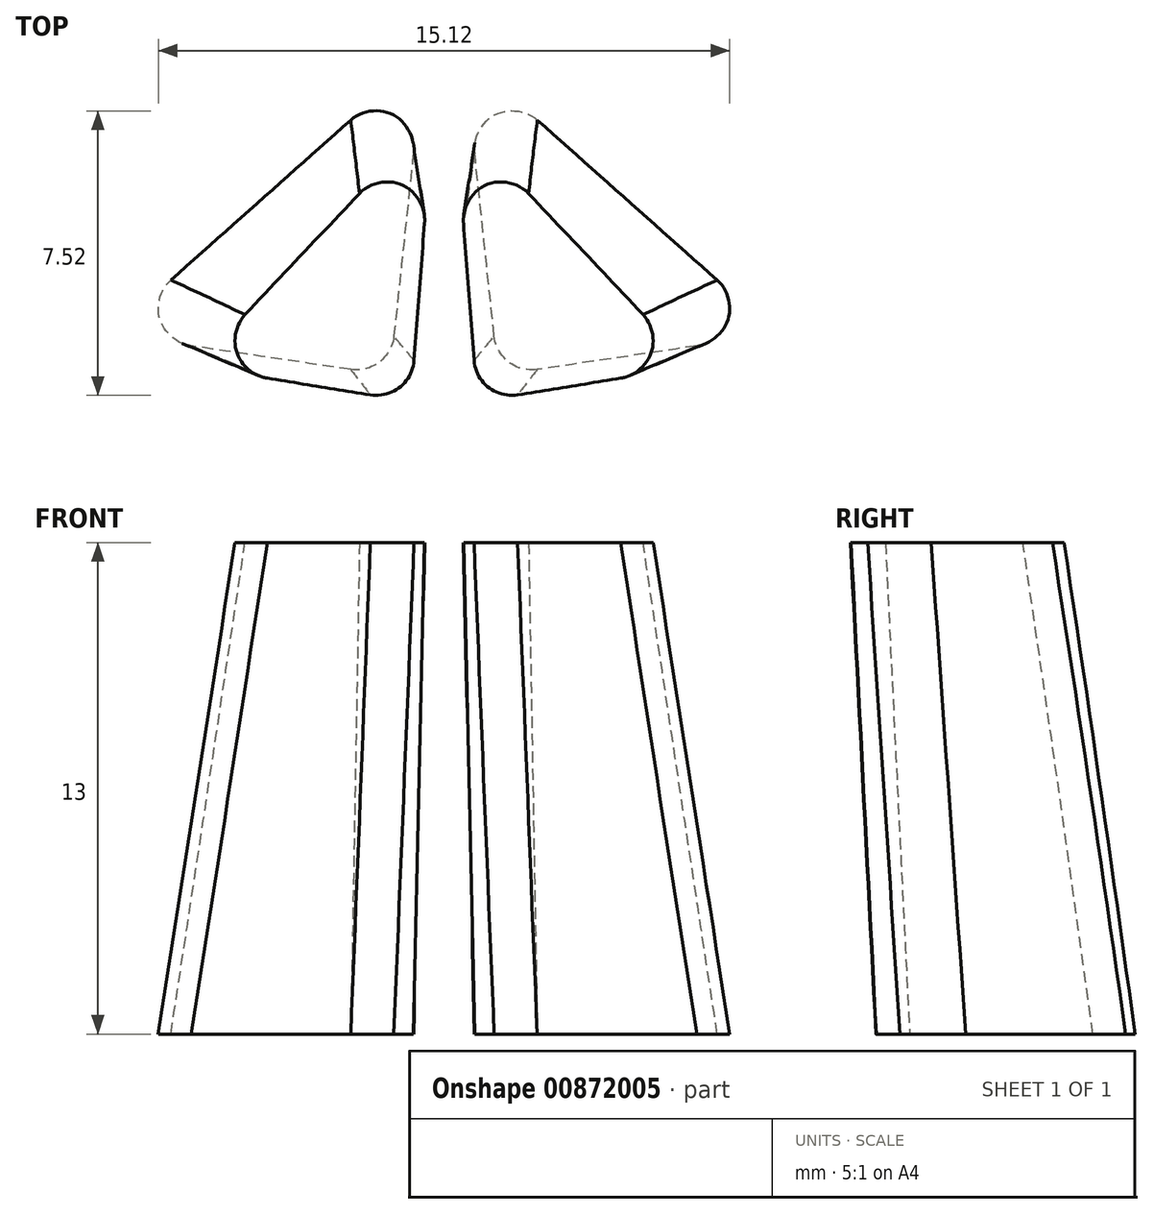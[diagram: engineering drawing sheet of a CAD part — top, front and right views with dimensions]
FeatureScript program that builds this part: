
annotation { "Feature Type Name" : "Feature", "Feature Type Description" : "" }
export const myFeature = defineFeature(function(context is Context, id is Id, definition is map)
    precondition{}
    {
        {
            var Q0;
            Q0=qCreatedBy(makeId("Top.planeOp"),FACE);
            var sketch = newSketch(context, id + "F0", { "sketchPlane" : qUnion([Q0])});
            skLineSegment(sketch, "E0", {"start": v(-1.48, -1.1) * mm, "end": v(-9, 0) * mm});
            skLineSegment(sketch, "E1", {"start": v(-9, 0) * mm, "end": v(-0.55, 7.43) * mm});
            skLineSegment(sketch, "E2", {"start": v(-0.55, 7.43) * mm, "end": v(-1.48, -1.1) * mm});
            skLineSegment(sketch, "E3", {"start": v(9.66, 0) * mm, "end": v(-11.81, 0) * mm, "construction": true});
            skCircle(sketch, "E4", {"center": v(0, 0) * mm, "radius": 10.65 * mm});
            skSolve(sketch);
        }
        {
            var Q0;
            Q0=qCreatedBy(makeId("Top.planeOp"),FACE);
            cPlane(context, id + "F1", {"entities" : qUnion([Q0]), "cplaneType" : CPlaneType.OFFSET, "offset" : 15 * mm, "width" : 150 * mm, "height" : 150 * mm});
        }
        {
            var Q0;
            Q0=qCreatedBy(id+"F1.planeOp",FACE);
            var sketch = newSketch(context, id + "F2", { "sketchPlane" : qUnion([Q0])});
            skLineSegment(sketch, "E5", {"start": v(-6.39, -1) * mm, "end": v(-0.28, 5.58) * mm});
            skLineSegment(sketch, "E6", {"start": v(-0.28, 5.58) * mm, "end": v(-0.83, -1.9) * mm});
            skLineSegment(sketch, "E7", {"start": v(-0.83, -1.9) * mm, "end": v(-6.39, -1) * mm});
            skLineSegment(sketch, "E8", {"start": v(7.96, 0) * mm, "end": v(-10.6, 0) * mm, "construction": true});
            skCircle(sketch, "E9", {"center": v(0, 0) * mm, "radius": 8.35 * mm});
            skSolve(sketch);
        }
        {
            var Q0;
            Q0=makeQuery(id+"F0.imprint","IMPRINT",FACE,{"disambiguationData":[TD([[makeQuery(id+"F0.imprint","IMPRINT",EDGE,{"derivedFrom":sQuery(id+"F0.wireOp",EDGE,"E0")}),-1.0]])]});
            var Q1;
            Q1=makeQuery(id+"F2.imprint","IMPRINT",FACE,{"disambiguationData":[TD([[makeQuery(id+"F2.imprint","IMPRINT",EDGE,{"derivedFrom":sQuery(id+"F2.wireOp",EDGE,"E5")}),-1.0]])]});
            loft(context, id + "F3", {"sheetProfilesArray" : [{ "sheetProfileEntities" : qUnion([Q0]) }, { "sheetProfileEntities" : qUnion([Q1]) }]});
        }
        {
            var Q0;
            Q0=makeQuery(id+"F3.opLoft","SWEPT_EDGE",EDGE,{"disambiguationData":[OSD([sQuery(id+"F0.wireOp",EDGE,"E1"),sQuery(id+"F0.wireOp",EDGE,"E2"),sQuery(id+"F2.wireOp",EDGE,"E5"),sQuery(id+"F2.wireOp",EDGE,"E6")])]});
            var Q1;
            Q1=makeQuery(id+"F3.opLoft","SWEPT_EDGE",EDGE,{"disambiguationData":[OSD([sQuery(id+"F0.wireOp",EDGE,"E0"),sQuery(id+"F0.wireOp",EDGE,"E1"),sQuery(id+"F2.wireOp",EDGE,"E5"),sQuery(id+"F2.wireOp",EDGE,"E7")])]});
            var Q2;
            Q2=makeQuery(id+"F3.opLoft","SWEPT_EDGE",EDGE,{"disambiguationData":[OSD([sQuery(id+"F0.wireOp",EDGE,"E0"),sQuery(id+"F0.wireOp",EDGE,"E2"),sQuery(id+"F2.wireOp",EDGE,"E6"),sQuery(id+"F2.wireOp",EDGE,"E7")])]});
            fillet(context, id + "F4", {"entities" : qUnion([Q0, Q1, Q2]), "radius" : 1 * mm, "tangentPropagation" : true, "allowEdgeOverflow" : false});
        }
        {
            var Q0;
            Q0=qCreatedBy(makeId("Right.planeOp"),FACE);
            cPlane(context, id + "F5", {"entities" : qUnion([Q0]), "cplaneType" : CPlaneType.OFFSET, "offset" : 0 * mm, "width" : 150 * mm, "height" : 150 * mm});
        }
        {
            var Q0;
            Q0=makeQuery(id+"F3.opLoft","SWEPT_BODY",BODY,{"disambiguationData":[OSD([makeQuery(id+"F0.imprint","IMPRINT",FACE,{"disambiguationData":[TD([[makeQuery(id+"F0.imprint","IMPRINT",EDGE,{"derivedFrom":sQuery(id+"F0.wireOp",EDGE,"E0")}),-1.0]])]}),makeQuery(id+"F2.imprint","IMPRINT",FACE,{"disambiguationData":[TD([[makeQuery(id+"F2.imprint","IMPRINT",EDGE,{"derivedFrom":sQuery(id+"F2.wireOp",EDGE,"E5")}),-1.0]])]})])]});
            var Q1;
            Q1=qCreatedBy(id+"F5.planeOp",FACE);
            mirror(context, id + "F6", {"entities" : qUnion([Q0]), "mirrorPlane" : qUnion([Q1])});
        }
        {
            var Q0;
            Q0=makeQuery(id+"F0.imprint","IMPRINT",FACE,{"disambiguationData":[TD([[makeQuery(id+"F0.imprint","IMPRINT",EDGE,{"derivedFrom":sQuery(id+"F0.wireOp",EDGE,"E0")}),1.0]])]});
            var Q1;
            Q1=makeQuery(id+"F0.imprint","IMPRINT",FACE,{"disambiguationData":[TD([[makeQuery(id+"F0.imprint","IMPRINT",EDGE,{"derivedFrom":sQuery(id+"F0.wireOp",EDGE,"E0")}),-1.0]])]});
            extrude(context, id + "F7", {"entities" : qUnion([Q0, Q1]), "operationType" : NewBodyOperationType.REMOVE, "depth" : 1 * mm, "offsetDistance" : 25 * mm});
        }
        {
            var Q0;
            Q0=makeQuery(id+"F2.imprint","IMPRINT",FACE,{"disambiguationData":[TD([[makeQuery(id+"F2.imprint","IMPRINT",EDGE,{"derivedFrom":sQuery(id+"F2.wireOp",EDGE,"E5")}),1.0]])]});
            var Q1;
            Q1=makeQuery(id+"F2.imprint","IMPRINT",FACE,{"disambiguationData":[TD([[makeQuery(id+"F2.imprint","IMPRINT",EDGE,{"derivedFrom":sQuery(id+"F2.wireOp",EDGE,"E5")}),-1.0]])]});
            extrude(context, id + "F8", {"entities" : qUnion([Q0, Q1]), "operationType" : NewBodyOperationType.REMOVE, "oppositeDirection" : true, "depth" : 1 * mm, "offsetDistance" : 25 * mm});
        }
    });
